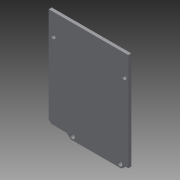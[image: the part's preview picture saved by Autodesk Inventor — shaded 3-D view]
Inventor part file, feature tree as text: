
AUTODESK INVENTOR PART (.ipt)
format: ipt  version: 2015 SP2 (Build 190223200, 223)  size: 105,472 bytes
history: native  units: mm
features: sketch x4, hole x2, extrude x1
ambient origin geometry x8: Origin, YZ Plane, XZ Plane, XY Plane, X Axis, Y Axis, Z Axis, Center Point
bodies: Solid1 (feature_tree)
feature tree (7):
  extrude  "Extrusion1"  Depth=2.0mm
  sketch  "Sketch2"  dims[d8=3.2mm d9=6.0mm d10=4.0mm d11=2.0mm d12=90.0deg d13=8.0mm d14=20.594885mm]
  sketch  "Sketch3"  dims[d15=3.2mm d16=6.0mm d17=4.0mm d18=2.0mm d19=90.0deg d20=8.0mm d21=20.594885mm]
  hole  "Hole1"  [1 undecoded]
  hole  "Hole2"  [1 undecoded]
  sketch  "Sketch5"
  sketch  "Sketch1"  dims[d3=2.0mm d4=0.0mm d5=3.2mm]
note: 2 required parameter values undecoded (feature->parameter linkage not recoverable at this tier; creation-order binding heuristic only, values carry confidence <= 0.55)
